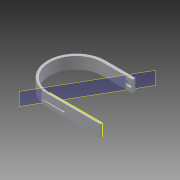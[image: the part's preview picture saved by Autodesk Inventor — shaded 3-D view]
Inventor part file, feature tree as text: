
AUTODESK INVENTOR PART (.ipt)
format: ipt  version: 2013 (Build 170138000, 138)  size: 166,400 bytes
history: native  units: mm
features: sketch x8, extrude x7, projected_geometry x3, plane x2
ambient origin geometry x8: Origin, YZ Plane, XZ Plane, XY Plane, X Axis, Y Axis, Z Axis, Center Point
bodies: Solid1 (feature_tree)
feature tree (20):
  extrude  "Extrusion1"  Depth=3.5mm
  sketch  "Sketch2"  dims[d2=50.8mm d3=5.0mm]
  extrude  "Extrusion2"  Depth=5.0mm
  plane  "Work Plane1"
  extrude  "Extrusion3"  Depth=20.0mm TaperAngle=0.0deg
  extrude  "Extrusion4"  Depth=7.0mm
  plane  "Work Plane2"
  extrude  "Extrusion5"  Depth=3.0mm TaperAngle=0.0deg
  extrude  "Extrusion6"  Depth=3.0mm
  extrude  "Extrusion7"  Depth=7.0mm
  sketch  "Sketch1"  dims[d0=88.9mm d1=3.5mm]
  sketch  "Sketch3"  dims[d4=88.9mm d6=20.0mm d7=0.0mm]
  sketch  "Sketch4"  dims[d8=7.0mm d9=7.0mm]
  sketch  "Sketch5"  dims[d10=44.45mm d11=3.0mm d12=0.0mm]
  sketch  "Sketch6"  dims[d13=150.0deg d14=3.0mm]
  sketch  "Sketch7"  dims[d15=30.0mm d16=0.0mm d17=7.0mm]
  sketch  "Sketch8"  dims[d18=7.0mm d19=44.45mm d20=12.0mm d21=12.0mm d22=3.0mm d23=0.0mm d24=105.0deg d25=3.0mm d26=0.0mm d27=3.0mm d28=0.0mm d29=1.5mm d30=0.0mm]
  projected_geometry  "Project Cut Edges1"
  projected_geometry  "Project Cut Edges2"
  projected_geometry  "Project Cut Edges3"
